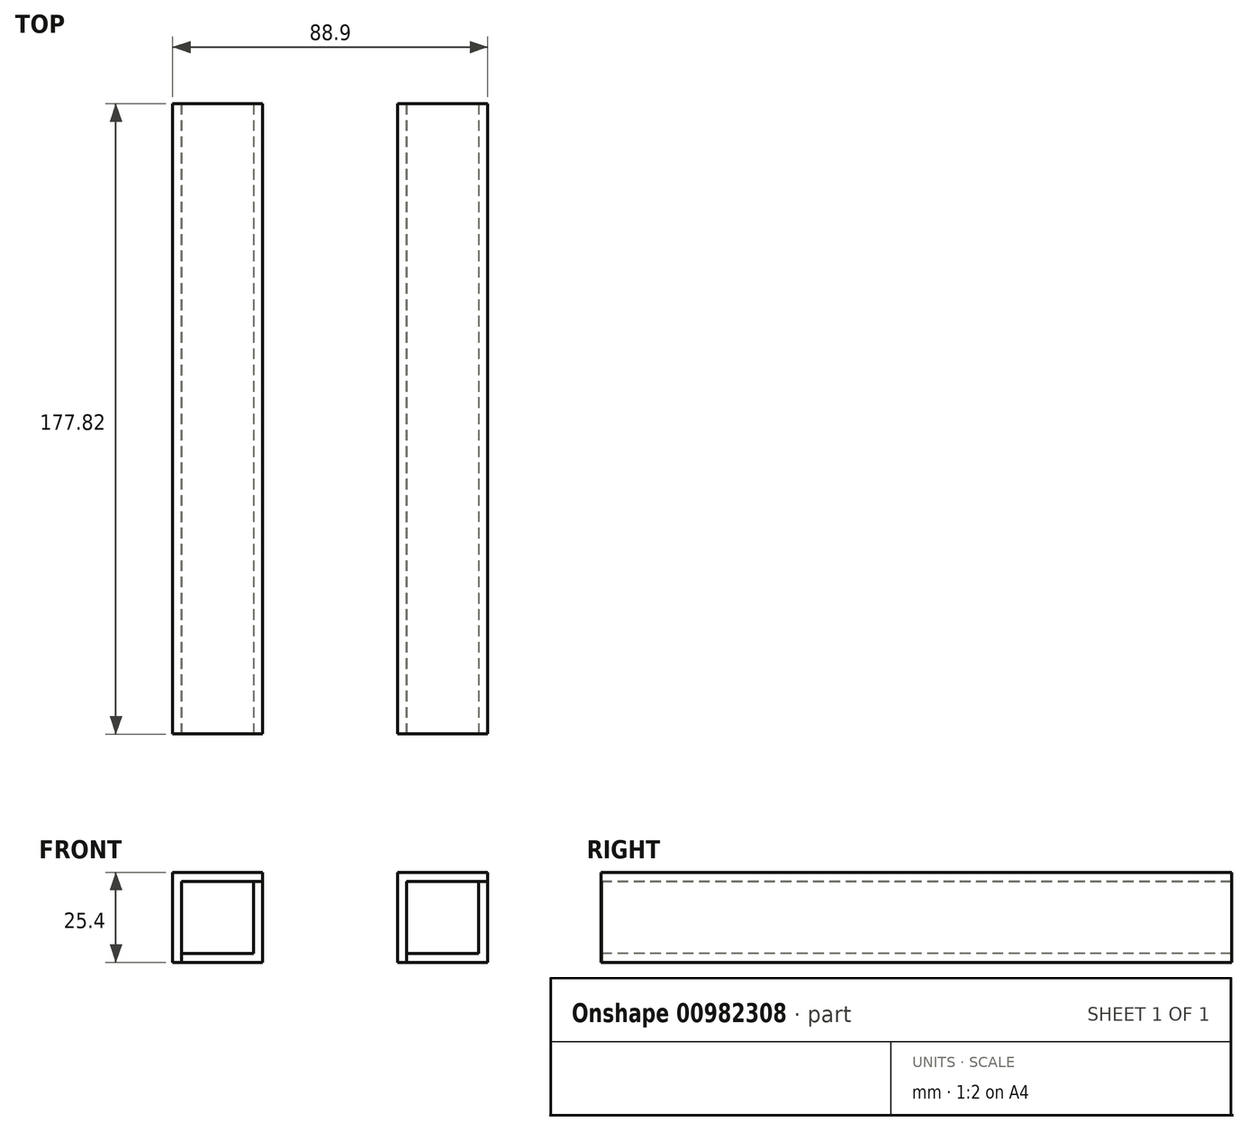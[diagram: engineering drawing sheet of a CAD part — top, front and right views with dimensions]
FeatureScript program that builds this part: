
annotation { "Feature Type Name" : "Feature", "Feature Type Description" : "" }
export const myFeature = defineFeature(function(context is Context, id is Id, definition is map)
    precondition{}
    {
        {
            var Q0;
            Q0=qCreatedBy(makeId("Top.planeOp"),FACE);
            var sketch = newSketch(context, id + "F0", { "sketchPlane" : qUnion([Q0])});
            skLineSegment(sketch, "E0.bottom", {"start": v(-39.86, 110.26) * mm, "end": v(-19.54, 110.26) * mm});
            skLineSegment(sketch, "E0.top", {"start": v(-39.86, -42.14) * mm, "end": v(-19.54, -42.14) * mm});
            skLineSegment(sketch, "E0.left", {"start": v(-39.86, 110.26) * mm, "end": v(-39.86, -42.14) * mm});
            skLineSegment(sketch, "E0.right", {"start": v(-19.54, 110.26) * mm, "end": v(-19.54, -42.14) * mm});
            skLineSegment(sketch, "E1.bottom", {"start": v(-19.54, 110.26) * mm, "end": v(-17, 110.26) * mm});
            skLineSegment(sketch, "E1.top", {"start": v(-19.54, -42.14) * mm, "end": v(-17, -42.14) * mm});
            skLineSegment(sketch, "E1.right", {"start": v(-17, 110.26) * mm, "end": v(-17, -42.14) * mm});
            skLineSegment(sketch, "E2.bottom", {"start": v(-39.86, 110.26) * mm, "end": v(-42.4, 110.26) * mm});
            skLineSegment(sketch, "E2.top", {"start": v(-39.86, -42.16) * mm, "end": v(-42.4, -42.16) * mm});
            skLineSegment(sketch, "E2.left", {"start": v(-39.86, 110.26) * mm, "end": v(-39.86, -42.16) * mm});
            skLineSegment(sketch, "E2.right", {"start": v(-42.4, 110.26) * mm, "end": v(-42.4, -42.16) * mm});
            skSolve(sketch);
        }
        {
            var Q0;
            {var subQ0=sQuery(id+"F0.wireOp",EDGE,"E0.bottom");Q0=makeQuery(id+"F0.imprint","IMPRINT",FACE,{"disambiguationData":[TD([[makeQuery(id+"F0.imprint","IMPRINT",EDGE,{"derivedFrom":subQ0}),-1.0]])]});}
            extrude(context, id + "F1", {"entities" : qUnion([Q0]), "depth" : 2.54 * mm, "offsetDistance" : 25.4 * mm});
        }
        {
            var Q0;
            {var subQ3=sQuery(id+"F0.wireOp",EDGE,"E2.bottom");Q0=makeQuery(id+"F0.imprint","IMPRINT",FACE,{"disambiguationData":[TD([[makeQuery(id+"F0.imprint","IMPRINT",EDGE,{"derivedFrom":subQ3}),1.0]])]});}
            var Q1;
            Q1=makeQuery(id+"F0.imprint","IMPRINT",FACE,{"disambiguationData":[TD([[makeQuery(id+"F0.imprint","IMPRINT",EDGE,{"derivedFrom":sQuery(id+"F0.wireOp",EDGE,"E1.bottom")}),-1.0]])]});
            extrude(context, id + "F2", {"entities" : qUnion([Q0, Q1]), "operationType" : NewBodyOperationType.ADD, "depth" : 25.4 * mm, "offsetDistance" : 25.4 * mm});
        }
        {
            var Q0;
            Q0=makeQuery(id+"F2.opExtrude","SWEPT_FACE",FACE,{"disambiguationData":[OSD([sQuery(id+"F0.wireOp",EDGE,"E2.left")])]});
            var sketch = newSketch(context, id + "F3", { "sketchPlane" : qUnion([Q0])});
            skLineSegment(sketch, "E3", {"start": v(-42.16, 22.86) * mm, "end": v(110.26, 22.86) * mm});
            skSolve(sketch);
        }
        {
            var Q0;
            {var subQ0=sQuery(id+"F3.wireOp",EDGE,"E3");Q0=makeQuery(id+"F3.imprint","IMPRINT",FACE,{"disambiguationData":[TD([[makeQuery(id+"F3.imprint","IMPRINT",EDGE,{"derivedFrom":subQ0}),1.0]])]});}
            extrude(context, id + "F4", {"entities" : qUnion([Q0]), "operationType" : NewBodyOperationType.ADD, "depth" : 22.86 * mm, "offsetDistance" : 25.4 * mm});
        }
        {
            var Q0;
            Q0=makeQuery(id+"F1.opExtrude","SWEPT_BODY",BODY,{"disambiguationData":[OSD([sQuery(id+"F0.wireOp",EDGE,"E0.bottom"),sQuery(id+"F0.wireOp",EDGE,"E0.top"),sQuery(id+"F0.wireOp",EDGE,"E0.right"),sQuery(id+"F0.wireOp",EDGE,"E2.left")])]});
            transform(context, id + "F5", {"entities" : qUnion([Q0]), "transformType" : TransformType.TRANSLATION_3D, "dx" : 63.5 * mm, "dy" : 0 * mm, "dz" : 0 * mm, "makeCopy" : true});
        }
        {
            var Q0;
            {var subQ0=sQuery(id+"F0.wireOp",EDGE,"E2.bottom");var subQ1=sQuery(id+"F0.wireOp",EDGE,"E0.bottom");Q0=makeQuery(id+"F5.opPattern","COPY",FACE,{"derivedFrom":makeQuery(id+"F4.boolean.opBoolean","MERGE",FACE,{"derivedFrom":[makeQuery(id+"F2.boolean.opBoolean","MERGE",FACE,{"derivedFrom":[makeQuery(id+"F1.opExtrude","SWEPT_FACE",FACE,{"disambiguationData":[OSD([subQ1])]}),makeQuery(id+"F2.opExtrude","SWEPT_FACE",FACE,{"disambiguationData":[OSD([sQuery(id+"F0.wireOp",EDGE,"E1.bottom")])]}),makeQuery(id+"F2.opExtrude","SWEPT_FACE",FACE,{"disambiguationData":[OSD([subQ0])]})]}),makeQuery(id+"F4.opExtrude","SWEPT_FACE",FACE,{"disambiguationData":[OSD([subQ1,subQ0,sQuery(id+"F0.wireOp",EDGE,"E2.left")])]})]}),"instanceName":"1"});}
            var Q1;
            {var subQ0=sQuery(id+"F0.wireOp",EDGE,"E2.bottom");var subQ1=sQuery(id+"F0.wireOp",EDGE,"E0.bottom");Q1=makeQuery(id+"F4.boolean.opBoolean","MERGE",FACE,{"derivedFrom":[makeQuery(id+"F2.boolean.opBoolean","MERGE",FACE,{"derivedFrom":[makeQuery(id+"F1.opExtrude","SWEPT_FACE",FACE,{"disambiguationData":[OSD([subQ1])]}),makeQuery(id+"F2.opExtrude","SWEPT_FACE",FACE,{"disambiguationData":[OSD([sQuery(id+"F0.wireOp",EDGE,"E1.bottom")])]}),makeQuery(id+"F2.opExtrude","SWEPT_FACE",FACE,{"disambiguationData":[OSD([subQ0])]})]}),makeQuery(id+"F4.opExtrude","SWEPT_FACE",FACE,{"disambiguationData":[OSD([subQ1,subQ0,sQuery(id+"F0.wireOp",EDGE,"E2.left")])]})]});}
            extrude(context, id + "F6", {"entities" : qUnion([Q0, Q1]), "operationType" : NewBodyOperationType.ADD, "depth" : 25.4 * mm, "offsetDistance" : 25.4 * mm});
        }
    });
